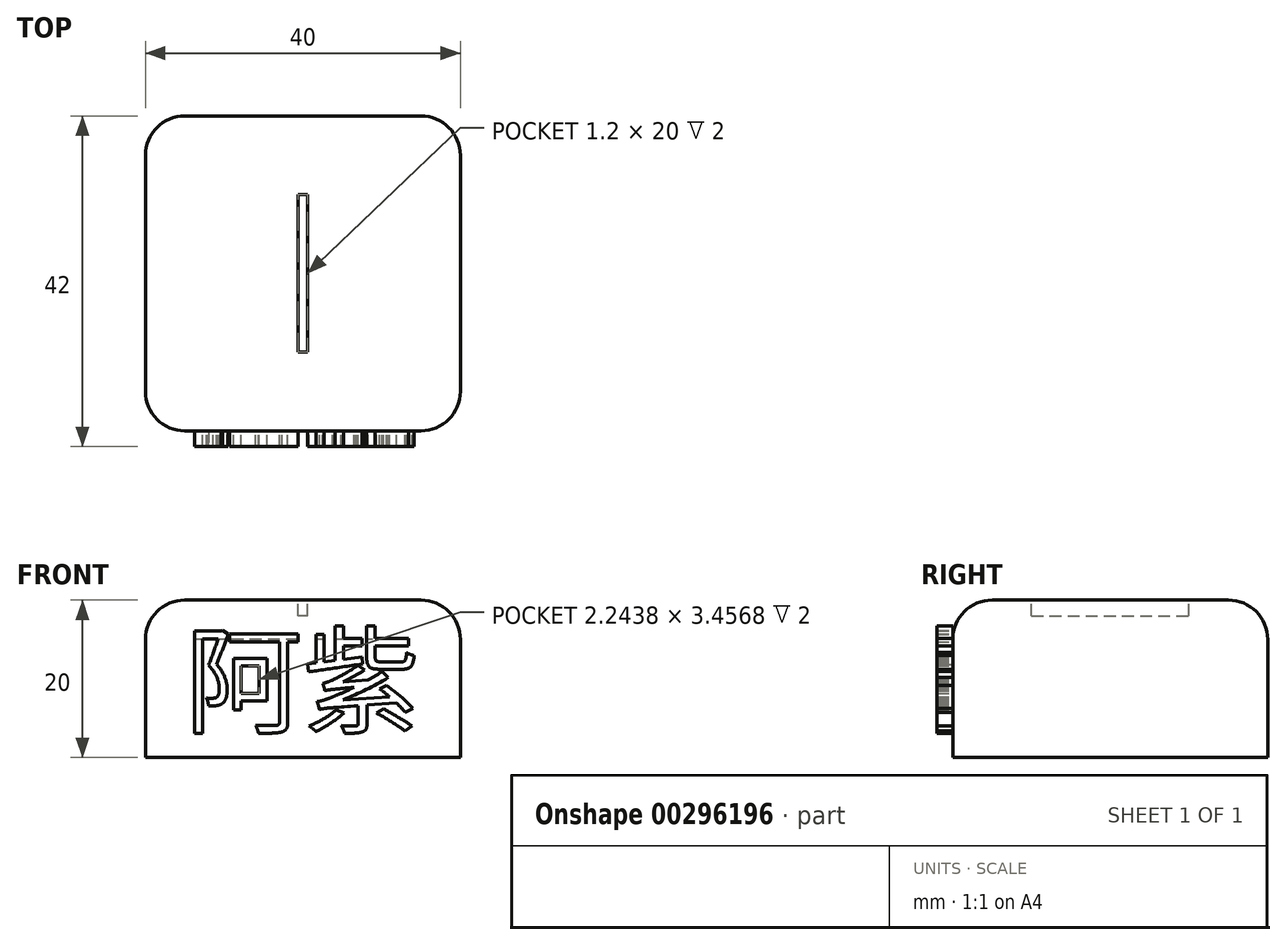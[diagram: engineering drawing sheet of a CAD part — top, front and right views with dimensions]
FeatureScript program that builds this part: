
annotation { "Feature Type Name" : "Feature", "Feature Type Description" : "" }
export const myFeature = defineFeature(function(context is Context, id is Id, definition is map)
    precondition{}
    {
        {
            var Q0;
            Q0=qCreatedBy(makeId("Top.planeOp"),FACE);
            var sketch = newSketch(context, id + "F0", { "sketchPlane" : qUnion([Q0])});
            skLineSegment(sketch, "E0.bottom", {"start": v(20, -20) * mm, "end": v(-20, -20) * mm});
            skLineSegment(sketch, "E0.top", {"start": v(20, 20) * mm, "end": v(-20, 20) * mm});
            skLineSegment(sketch, "E0.left", {"start": v(20, -20) * mm, "end": v(20, 20) * mm});
            skLineSegment(sketch, "E0.right", {"start": v(-20, -20) * mm, "end": v(-20, 20) * mm});
            skPoint(sketch, "E0.middle", {"position": v(0, 0) * mm});
            skLineSegment(sketch, "E1.bottom", {"start": v(0.6, -10) * mm, "end": v(-0.6, -10) * mm});
            skLineSegment(sketch, "E1.top", {"start": v(0.6, 10) * mm, "end": v(-0.6, 10) * mm});
            skLineSegment(sketch, "E1.left", {"start": v(0.6, -10) * mm, "end": v(0.6, 10) * mm});
            skLineSegment(sketch, "E1.right", {"start": v(-0.6, -10) * mm, "end": v(-0.6, 10) * mm});
            skSolve(sketch);
        }
        {
            var Q0;
            Q0=makeQuery(id+"F0.imprint","IMPRINT",FACE,{"disambiguationData":[TD([[makeQuery(id+"F0.imprint","IMPRINT",EDGE,{"derivedFrom":sQuery(id+"F0.wireOp",EDGE,"E0.bottom")}),-1.0]])]});
            var Q1;
            Q1=makeQuery(id+"F0.imprint","IMPRINT",FACE,{"disambiguationData":[TD([[makeQuery(id+"F0.imprint","IMPRINT",EDGE,{"derivedFrom":sQuery(id+"F0.wireOp",EDGE,"E1.bottom")}),-1.0]])]});
            extrude(context, id + "F1", {"entities" : qUnion([Q0, Q1]), "oppositeDirection" : true, "depth" : 20 * mm});
        }
        {
            var Q0;
            Q0=makeQuery(id+"F0.imprint","IMPRINT",FACE,{"disambiguationData":[TD([[makeQuery(id+"F0.imprint","IMPRINT",EDGE,{"derivedFrom":sQuery(id+"F0.wireOp",EDGE,"E1.bottom")}),-1.0]])]});
            extrude(context, id + "F2", {"entities" : qUnion([Q0]), "operationType" : NewBodyOperationType.REMOVE, "oppositeDirection" : true, "depth" : 2 * mm});
        }
        {
            var Q0;
            Q0=makeQuery(id+"F2.boolean.opBoolean","COPY",EDGE,{"derivedFrom":makeQuery(id+"F2.opExtrude","CAP_EDGE",EDGE,{"disambiguationData":[OSD([sQuery(id+"F0.wireOp",EDGE,"E1.left")])],"isStart":true})});
            var Q1;
            Q1=makeQuery(id+"F2.boolean.opBoolean","COPY",EDGE,{"derivedFrom":makeQuery(id+"F2.opExtrude","CAP_EDGE",EDGE,{"disambiguationData":[OSD([sQuery(id+"F0.wireOp",EDGE,"E1.right")])],"isStart":true})});
            var Q2;
            Q2=makeQuery(id+"F1.opExtrude","SWEPT_EDGE",EDGE,{"disambiguationData":[OSD([sQuery(id+"F0.wireOp",EDGE,"E0.bottom"),sQuery(id+"F0.wireOp",EDGE,"E0.left")])]});
            var Q3;
            Q3=makeQuery(id+"F1.opExtrude","SWEPT_EDGE",EDGE,{"disambiguationData":[OSD([sQuery(id+"F0.wireOp",EDGE,"E0.top"),sQuery(id+"F0.wireOp",EDGE,"E0.left")])]});
            var Q4;
            Q4=makeQuery(id+"F1.opExtrude","CAP_EDGE",EDGE,{"disambiguationData":[OSD([sQuery(id+"F0.wireOp",EDGE,"E0.left")])],"isStart":true});
            var Q5;
            Q5=makeQuery(id+"F1.opExtrude","SWEPT_EDGE",EDGE,{"disambiguationData":[OSD([sQuery(id+"F0.wireOp",EDGE,"E0.bottom"),sQuery(id+"F0.wireOp",EDGE,"E0.right")])]});
            var Q6;
            Q6=makeQuery(id+"F1.opExtrude","SWEPT_EDGE",EDGE,{"disambiguationData":[OSD([sQuery(id+"F0.wireOp",EDGE,"E0.top"),sQuery(id+"F0.wireOp",EDGE,"E0.right")])]});
            var Q7;
            Q7=makeQuery(id+"F1.opExtrude","CAP_EDGE",EDGE,{"disambiguationData":[OSD([sQuery(id+"F0.wireOp",EDGE,"E0.top")])],"isStart":true});
            var Q8;
            Q8=makeQuery(id+"F1.opExtrude","CAP_EDGE",EDGE,{"disambiguationData":[OSD([sQuery(id+"F0.wireOp",EDGE,"E0.right")])],"isStart":true});
            var Q9;
            Q9=makeQuery(id+"F1.opExtrude","CAP_EDGE",EDGE,{"disambiguationData":[OSD([sQuery(id+"F0.wireOp",EDGE,"E0.bottom")])],"isStart":true});
            fillet(context, id + "F3", {"entities" : qUnion([Q0, Q1, Q2, Q3, Q4, Q5, Q6, Q7, Q8, Q9]), "radius" : 5 * mm, "tangentPropagation" : true, "allowEdgeOverflow" : false});
        }
        {
            var Q0;
            Q0=makeQuery(id+"F1.opExtrude","SWEPT_FACE",FACE,{"disambiguationData":[OSD([sQuery(id+"F0.wireOp",EDGE,"E0.bottom")])]});
            var sketch = newSketch(context, id + "F4", { "sketchPlane" : qUnion([Q0])});
            skText(sketch, "E2", { "text": "阿紫", "fontName": "NotoSansCJKtc-Regular.otf"});
            const initialGuessF4  = {"E2": [-0.015, -0.01577, 1, 0, 0.01077]};
            skSetInitialGuess(sketch, initialGuessF4);
            skSolve(sketch);
        }
        {
            var Q0;
            Q0=makeQuery(id+"F4.imprint","IMPRINT",FACE,{"disambiguationData":[TD([[makeQuery(id+"F4.imprint","IMPRINT",EDGE,{"derivedFrom":sQuery(id+"F4.wireOp",EDGE,"E2.sketch_text.stroke-0")}),1.0]])]});
            var Q1;
            {var subQ7=sQuery(id+"F4.wireOp",EDGE,"E2.sketch_text.stroke-7");Q1=makeQuery(id+"F4.imprint","IMPRINT",FACE,{"disambiguationData":[TD([[makeQuery(id+"F4.imprint","IMPRINT",EDGE,{"derivedFrom":subQ7}),1.0]])]});}
            var Q2;
            {var subQ0=sQuery(id+"F4.wireOp",EDGE,"E2.sketch_text.stroke-3");Q2=makeQuery(id+"F4.imprint","IMPRINT",FACE,{"disambiguationData":[TD([[makeQuery(id+"F4.imprint","IMPRINT",EDGE,{"derivedFrom":subQ0}),1.0]])]});}
            var Q3;
            {var subQ0=sQuery(id+"F4.wireOp",EDGE,"E2.sketch_text.stroke-28");Q3=makeQuery(id+"F4.imprint","IMPRINT",FACE,{"disambiguationData":[TD([[makeQuery(id+"F4.imprint","IMPRINT",EDGE,{"derivedFrom":subQ0}),1.0]])]});}
            var Q4;
            {var subQ1=sQuery(id+"F4.wireOp",EDGE,"E2.sketch_text.stroke-30");Q4=makeQuery(id+"F4.imprint","IMPRINT",FACE,{"disambiguationData":[TD([[makeQuery(id+"F4.imprint","IMPRINT",EDGE,{"derivedFrom":subQ1}),1.0]])]});}
            var Q5;
            Q5=makeQuery(id+"F4.imprint","IMPRINT",FACE,{"disambiguationData":[TD([[makeQuery(id+"F4.imprint","IMPRINT",EDGE,{"derivedFrom":sQuery(id+"F4.wireOp",EDGE,"E2.sketch_text.stroke-18")}),1.0]])]});
            var Q6;
            Q6=makeQuery(id+"F4.imprint","IMPRINT",FACE,{"disambiguationData":[TD([[makeQuery(id+"F4.imprint","IMPRINT",EDGE,{"derivedFrom":sQuery(id+"F4.wireOp",EDGE,"E2.sketch_text.stroke-54")}),1.0]])]});
            var Q7;
            {var subQ0=sQuery(id+"F4.wireOp",EDGE,"E2.sketch_text.stroke-64");Q7=makeQuery(id+"F4.imprint","IMPRINT",FACE,{"disambiguationData":[TD([[makeQuery(id+"F4.imprint","IMPRINT",EDGE,{"derivedFrom":subQ0}),1.0]])]});}
            var Q8;
            {var subQ1=sQuery(id+"F4.wireOp",EDGE,"E2.sketch_text.stroke-58");Q8=makeQuery(id+"F4.imprint","IMPRINT",FACE,{"disambiguationData":[TD([[makeQuery(id+"F4.imprint","IMPRINT",EDGE,{"derivedFrom":subQ1}),1.0]])]});}
            var Q9;
            {var subQ1=sQuery(id+"F4.wireOp",EDGE,"E2.sketch_text.stroke-48");Q9=makeQuery(id+"F4.imprint","IMPRINT",FACE,{"disambiguationData":[TD([[makeQuery(id+"F4.imprint","IMPRINT",EDGE,{"derivedFrom":subQ1}),1.0]])]});}
            var Q10;
            Q10=makeQuery(id+"F4.imprint","IMPRINT",FACE,{"disambiguationData":[TD([[makeQuery(id+"F4.imprint","IMPRINT",EDGE,{"derivedFrom":sQuery(id+"F4.wireOp",EDGE,"E2.sketch_text.stroke-40")}),1.0]])]});
            var Q11;
            Q11=makeQuery(id+"F4.imprint","IMPRINT",FACE,{"disambiguationData":[TD([[makeQuery(id+"F4.imprint","IMPRINT",EDGE,{"derivedFrom":sQuery(id+"F4.wireOp",EDGE,"E2.sketch_text.stroke-78")}),1.0]])]});
            var Q12;
            Q12=makeQuery(id+"F4.imprint","IMPRINT",FACE,{"disambiguationData":[TD([[makeQuery(id+"F4.imprint","IMPRINT",EDGE,{"derivedFrom":sQuery(id+"F4.wireOp",EDGE,"E2.sketch_text.stroke-70")}),1.0]])]});
            var Q13;
            Q13=makeQuery(id+"F4.imprint","IMPRINT",FACE,{"disambiguationData":[TD([[makeQuery(id+"F4.imprint","IMPRINT",EDGE,{"derivedFrom":sQuery(id+"F4.wireOp",EDGE,"E2.sketch_text.stroke-74")}),1.0]])]});
            extrude(context, id + "F5", {"entities" : qUnion([Q0, Q1, Q2, Q3, Q4, Q5, Q6, Q7, Q8, Q9, Q10, Q11, Q12, Q13]), "operationType" : NewBodyOperationType.ADD, "depth" : 2 * mm});
        }
    });
